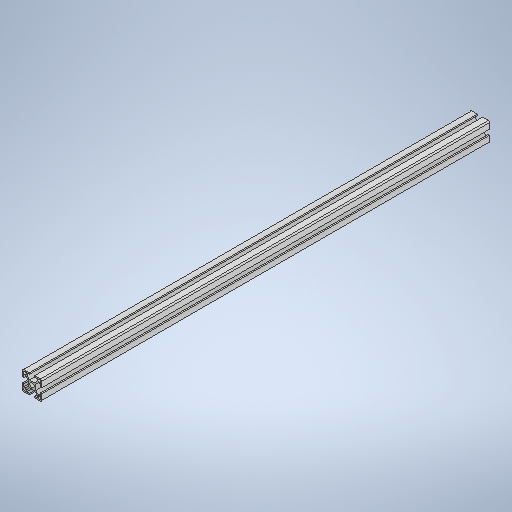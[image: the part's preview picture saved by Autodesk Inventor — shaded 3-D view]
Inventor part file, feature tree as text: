
AUTODESK INVENTOR PART (.ipt)
format: ipt  version: 2025 (Build 290162000, 162)  size: 313,344 bytes
history: native  units: in
note: dims shown in document units (in); Inventor stores cm internally (conversion verified against a paired STEP export)
features: extrude x1, sketch x1
ambient origin geometry x8: Origin, YZ Plane, XZ Plane, XY Plane, X Axis, Y Axis, Z Axis, Center Point
bodies: Solid1 (feature_tree)
feature tree (2):
  extrude  "Extrusion1"  Depth=27.5591in
  sketch  "Sketch1"  dims[d6=27.5591in d7=0.0in d8=0.1969in d9=0.0344in]
